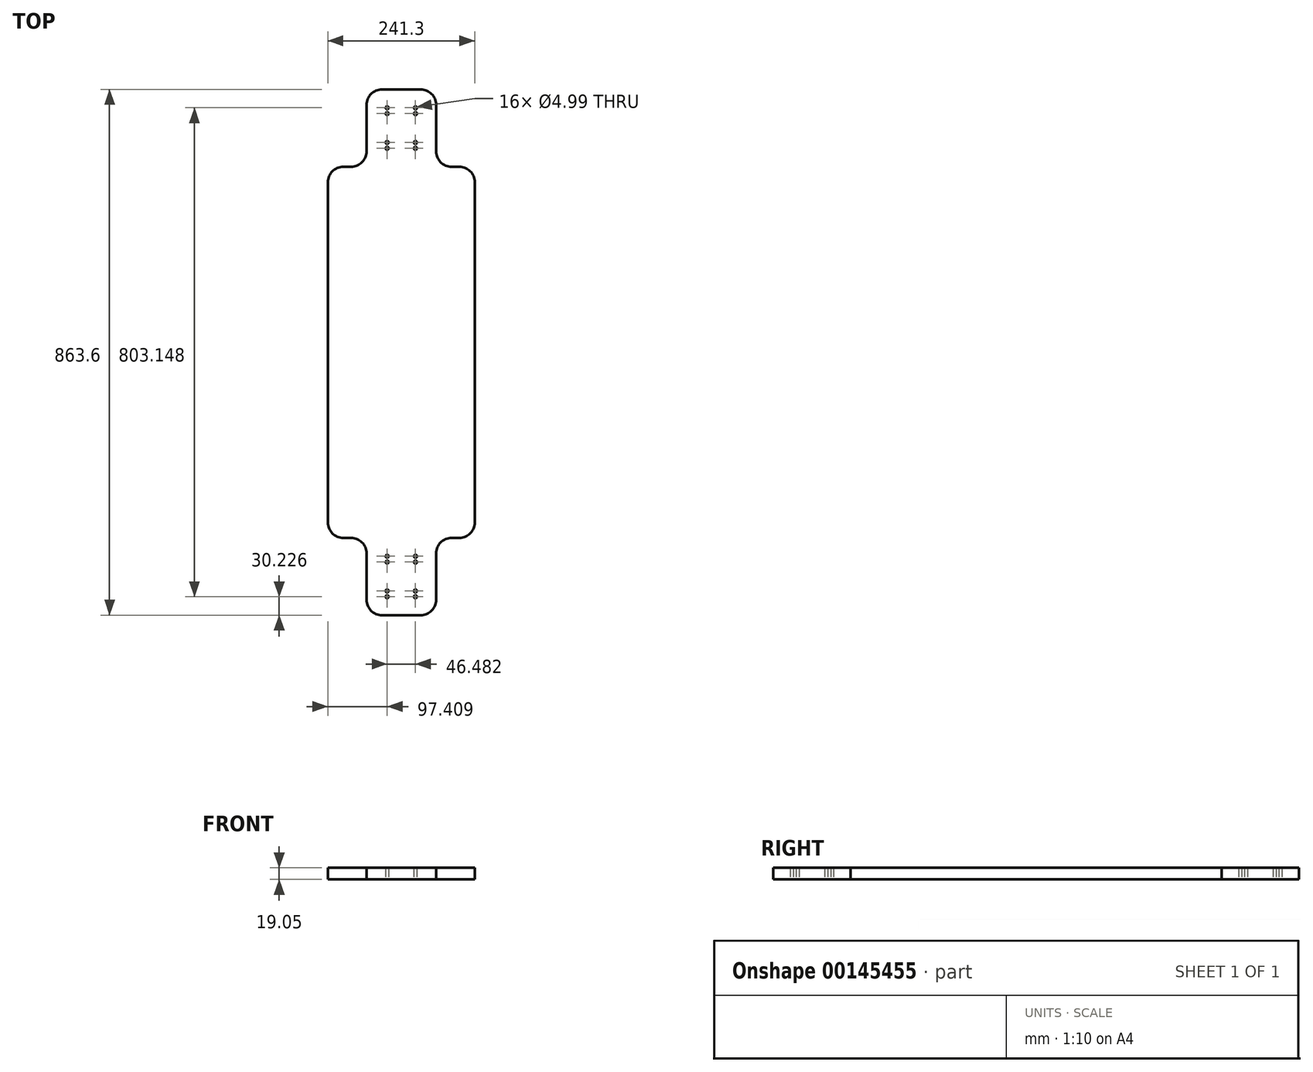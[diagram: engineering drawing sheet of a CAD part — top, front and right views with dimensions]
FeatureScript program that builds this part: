
annotation { "Feature Type Name" : "Feature", "Feature Type Description" : "" }
export const myFeature = defineFeature(function(context is Context, id is Id, definition is map)
    precondition{}
    {
        {
            var Q0;
            Q0=qCreatedBy(makeId("Top.planeOp"),FACE);
            var sketch = newSketch(context, id + "F0", { "sketchPlane" : qUnion([Q0])});
            skLineSegment(sketch, "E0.bottom", {"start": v(82.55, 304.8) * mm, "end": v(95.25, 304.8) * mm});
            skLineSegment(sketch, "E0.top", {"start": v(-95.25, -304.8) * mm, "end": v(-82.55, -304.8) * mm});
            skLineSegment(sketch, "E0.left", {"start": v(-120.65, 279.4) * mm, "end": v(-120.65, -279.4) * mm});
            skLineSegment(sketch, "E0.right", {"start": v(120.65, 279.4) * mm, "end": v(120.65, -279.4) * mm});
            skPoint(sketch, "E0.middle", {"position": v(0, 0) * mm});
            skLineSegment(sketch, "E1.top", {"start": v(-31.75, -431.8) * mm, "end": v(31.75, -431.8) * mm});
            skLineSegment(sketch, "E1.left", {"start": v(-57.15, -330.2) * mm, "end": v(-57.15, -406.4) * mm});
            skLineSegment(sketch, "E1.right", {"start": v(57.15, -330.2) * mm, "end": v(57.15, -406.4) * mm});
            skPoint(sketch, "E1.middle", {"position": v(0, -368.3) * mm});
            skLineSegment(sketch, "E2.MirrorCS", {"start": v(-95.25, 304.8) * mm, "end": v(-82.55, 304.8) * mm});
            skPoint(sketch, "E3.MirrorP", {"position": v(0, 368.3) * mm});
            skLineSegment(sketch, "E4.MirrorCS", {"start": v(-31.75, 431.8) * mm, "end": v(31.75, 431.8) * mm});
            skLineSegment(sketch, "E5.MirrorCS", {"start": v(57.15, 330.2) * mm, "end": v(57.15, 406.4) * mm});
            skLineSegment(sketch, "E6.MirrorCS", {"start": v(-57.15, 330.2) * mm, "end": v(-57.15, 406.4) * mm});
            skPoint(sketch, "E7.newPointA", {"position": v(-57.15, 304.8) * mm});
            skPoint(sketch, "E7.newPointB", {"position": v(120.65, 304.8) * mm});
            skArc(sketch, "E7.filletArc", {"start": v(-82.55, 304.8) * mm, "mid": v(-64.59, 312.24) * mm, "end": v(-57.15, 330.2) * mm});
            skPoint(sketch, "E8.newPointA", {"position": v(57.15, 304.8) * mm});
            skPoint(sketch, "E8.newPointB", {"position": v(-120.65, 304.8) * mm});
            skArc(sketch, "E8.filletArc", {"start": v(57.15, 330.2) * mm, "mid": v(64.59, 312.24) * mm, "end": v(82.55, 304.8) * mm});
            skPoint(sketch, "E9.visualSharp", {"position": v(-57.15, 431.8) * mm});
            skArc(sketch, "E9.filletArc", {"start": v(-31.75, 431.8) * mm, "mid": v(-49.71, 424.36) * mm, "end": v(-57.15, 406.4) * mm});
            skPoint(sketch, "E10.visualSharp", {"position": v(57.15, 431.8) * mm});
            skArc(sketch, "E10.filletArc", {"start": v(57.15, 406.4) * mm, "mid": v(49.71, 424.36) * mm, "end": v(31.75, 431.8) * mm});
            skArc(sketch, "E11.filletArc", {"start": v(-95.25, 304.8) * mm, "mid": v(-113.21, 297.36) * mm, "end": v(-120.65, 279.4) * mm});
            skArc(sketch, "E12.filletArc", {"start": v(120.65, 279.4) * mm, "mid": v(113.21, 297.36) * mm, "end": v(95.25, 304.8) * mm});
            skPoint(sketch, "E13.visualSharp", {"position": v(120.65, -304.8) * mm});
            skArc(sketch, "E13.filletArc", {"start": v(95.25, -304.8) * mm, "mid": v(113.21, -297.36) * mm, "end": v(120.65, -279.4) * mm});
            skLineSegment(sketch, "E14.trimOffspring", {"start": v(82.55, -304.8) * mm, "end": v(95.25, -304.8) * mm});
            skPoint(sketch, "E15.visualSharp", {"position": v(57.15, -304.8) * mm});
            skArc(sketch, "E15.filletArc", {"start": v(82.55, -304.8) * mm, "mid": v(64.59, -312.24) * mm, "end": v(57.15, -330.2) * mm});
            skPoint(sketch, "E16.visualSharp", {"position": v(57.15, -431.8) * mm});
            skArc(sketch, "E16.filletArc", {"start": v(31.75, -431.8) * mm, "mid": v(49.71, -424.36) * mm, "end": v(57.15, -406.4) * mm});
            skPoint(sketch, "E17.visualSharp", {"position": v(-57.15, -431.8) * mm});
            skArc(sketch, "E17.filletArc", {"start": v(-57.15, -406.4) * mm, "mid": v(-49.71, -424.36) * mm, "end": v(-31.75, -431.8) * mm});
            skPoint(sketch, "E18.visualSharp", {"position": v(-57.15, -304.8) * mm});
            skArc(sketch, "E18.filletArc", {"start": v(-57.15, -330.2) * mm, "mid": v(-64.59, -312.24) * mm, "end": v(-82.55, -304.8) * mm});
            skPoint(sketch, "E19.visualSharp", {"position": v(-120.65, -304.8) * mm});
            skArc(sketch, "E19.filletArc", {"start": v(-120.65, -279.4) * mm, "mid": v(-113.21, -297.36) * mm, "end": v(-95.25, -304.8) * mm});
            skLineSegment(sketch, "E20.bottom", {"start": v(-28.07, -330.2) * mm, "end": v(28.07, -330.2) * mm});
            skLineSegment(sketch, "E20.top", {"start": v(-28.07, -406.4) * mm, "end": v(28.07, -406.4) * mm});
            skLineSegment(sketch, "E20.left", {"start": v(-28.07, -330.2) * mm, "end": v(-28.07, -406.4) * mm});
            skLineSegment(sketch, "E20.right", {"start": v(28.07, -330.2) * mm, "end": v(28.07, -406.4) * mm});
            skLineSegment(sketch, "E21", {"start": v(-23.24, -330.2) * mm, "end": v(-23.24, -406.4) * mm, "construction": true});
            skLineSegment(sketch, "E22", {"start": v(-28.07, -401.57) * mm, "end": v(28.07, -401.57) * mm, "construction": true});
            skLineSegment(sketch, "E23", {"start": v(-28.07, -392.01) * mm, "end": v(28.07, -392.01) * mm, "construction": true});
            skCircle(sketch, "E24", {"center": v(-23.24, -392.01) * mm, "radius": 2.5 * mm});
            skCircle(sketch, "E25", {"center": v(-23.24, -401.57) * mm, "radius": 2.5 * mm});
            skLineSegment(sketch, "E26", {"start": v(-28.07, -368.3) * mm, "end": v(28.07, -368.3) * mm, "construction": true});
            skLineSegment(sketch, "E27", {"start": v(0, -330.2) * mm, "end": v(0, -406.4) * mm, "construction": true});
            skCircle(sketch, "E28.MirrorC", {"center": v(-23.24, -344.59) * mm, "radius": 2.5 * mm});
            skCircle(sketch, "E29.MirrorC", {"center": v(-23.24, -335.03) * mm, "radius": 2.5 * mm});
            skCircle(sketch, "E30.MirrorC", {"center": v(23.24, -392.01) * mm, "radius": 2.5 * mm});
            skCircle(sketch, "E31.MirrorC", {"center": v(23.24, -344.59) * mm, "radius": 2.5 * mm});
            skCircle(sketch, "E32.MirrorC", {"center": v(23.24, -335.03) * mm, "radius": 2.5 * mm});
            skCircle(sketch, "E33.MirrorC", {"center": v(23.24, -401.57) * mm, "radius": 2.5 * mm});
            skLineSegment(sketch, "E34.MirrorCS", {"start": v(23.24, -330.2) * mm, "end": v(23.24, -406.4) * mm, "construction": true});
            skCircle(sketch, "E35.MirrorC", {"center": v(-23.24, 335.03) * mm, "radius": 2.5 * mm});
            skCircle(sketch, "E36.MirrorC", {"center": v(-23.24, 344.59) * mm, "radius": 2.5 * mm});
            skCircle(sketch, "E37.MirrorC", {"center": v(23.24, 335.03) * mm, "radius": 2.5 * mm});
            skCircle(sketch, "E38.MirrorC", {"center": v(23.24, 344.59) * mm, "radius": 2.5 * mm});
            skCircle(sketch, "E39.MirrorC", {"center": v(23.24, 392.01) * mm, "radius": 2.5 * mm});
            skCircle(sketch, "E40.MirrorC", {"center": v(23.24, 401.57) * mm, "radius": 2.5 * mm});
            skCircle(sketch, "E41.MirrorC", {"center": v(-23.24, 401.57) * mm, "radius": 2.5 * mm});
            skCircle(sketch, "E42.MirrorC", {"center": v(-23.24, 392.01) * mm, "radius": 2.5 * mm});
            skSolve(sketch);
        }
        {
            var Q0;
            Q0=makeQuery(id+"F0.imprint","IMPRINT",FACE,{"disambiguationData":[TD([[makeQuery(id+"F0.imprint","IMPRINT",EDGE,{"derivedFrom":sQuery(id+"F0.wireOp",EDGE,"E0.bottom")}),-1.0]])]});
            var Q1;
            Q1=makeQuery(id+"F0.imprint","IMPRINT",FACE,{"disambiguationData":[TD([[makeQuery(id+"F0.imprint","IMPRINT",EDGE,{"derivedFrom":sQuery(id+"F0.wireOp",EDGE,"E20.bottom")}),-1.0]])]});
            extrude(context, id + "F1", {"entities" : qUnion([Q0, Q1]), "depth" : 19.05 * mm});
        }
    });
